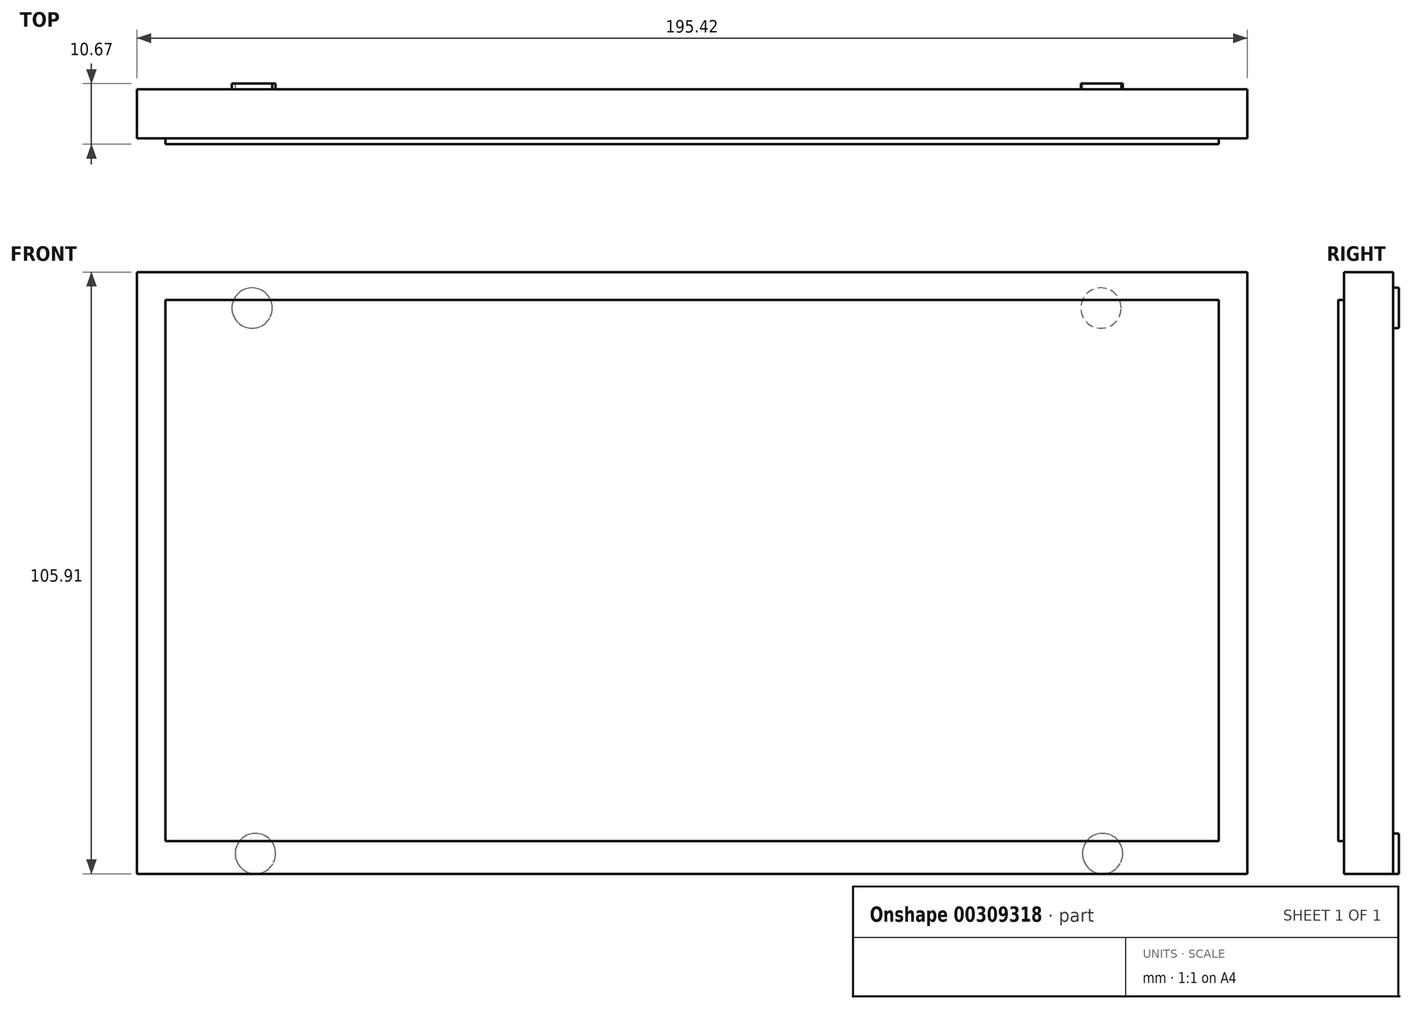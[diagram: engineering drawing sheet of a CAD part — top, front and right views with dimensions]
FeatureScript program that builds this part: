
annotation { "Feature Type Name" : "Feature", "Feature Type Description" : "" }
export const myFeature = defineFeature(function(context is Context, id is Id, definition is map)
    precondition{}
    {
        {
            var Q0;
            Q0=qCreatedBy(makeId("Front.planeOp"),FACE);
            var sketch = newSketch(context, id + "F0", { "sketchPlane" : qUnion([Q0])});
            skLineSegment(sketch, "E0.bottom", {"start": v(-95.26, 50.08) * mm, "end": v(100.16, 50.08) * mm});
            skLineSegment(sketch, "E0.top", {"start": v(-95.26, -55.83) * mm, "end": v(100.16, -55.83) * mm});
            skLineSegment(sketch, "E0.left", {"start": v(-95.26, 50.08) * mm, "end": v(-95.26, -55.83) * mm});
            skLineSegment(sketch, "E0.right", {"start": v(100.16, 50.08) * mm, "end": v(100.16, -55.83) * mm});
            skSolve(sketch);
        }
        {
            var Q0;
            Q0 = qSketchRegion(id + "F0", true);
            var Q1;
            Q1=makeQuery(id+"F0.imprint","IMPRINT",FACE,{"disambiguationData":[TD([[makeQuery(id+"F0.imprint","IMPRINT",EDGE,{"derivedFrom":sQuery(id+"F0.wireOp",EDGE,"Fiwb6U15-hAyw-maav-ymzA-u1ZgBlc6pZ0k.bottom")}),-1.0]])]});
            extrude(context, id + "F1", {"entities" : qUnion([Q0, Q1]), "depth" : 8.64 * mm});
        }
        {
            var Q0;
            Q0=makeQuery(id+"F1.opExtrude","CAP_FACE",FACE,{"disambiguationData":[OSD([sQuery(id+"F0.wireOp",EDGE,"E0.bottom"),sQuery(id+"F0.wireOp",EDGE,"E0.top"),sQuery(id+"F0.wireOp",EDGE,"E0.left"),sQuery(id+"F0.wireOp",EDGE,"E0.right")])],"isStart":false});
            var sketch = newSketch(context, id + "F2", { "sketchPlane" : qUnion([Q0])});
            skLineSegment(sketch, "E1.bottom", {"start": v(-90.23, 45.19) * mm, "end": v(95.12, 45.19) * mm});
            skLineSegment(sketch, "E1.top", {"start": v(-90.23, -50.08) * mm, "end": v(95.12, -50.08) * mm});
            skLineSegment(sketch, "E1.left", {"start": v(-90.23, 45.19) * mm, "end": v(-90.23, -50.08) * mm});
            skLineSegment(sketch, "E1.right", {"start": v(95.12, 45.19) * mm, "end": v(95.12, -50.08) * mm});
            skSolve(sketch);
        }
        {
            var Q0;
            Q0 = qSketchRegion(id + "F2", true);
            extrude(context, id + "F3", {"entities" : qUnion([Q0]), "operationType" : NewBodyOperationType.ADD, "depth" : 1.02 * mm});
        }
        {
            var Q0;
            Q0=makeQuery(id+"F1.opExtrude","CAP_FACE",FACE,{"disambiguationData":[OSD([sQuery(id+"F0.wireOp",EDGE,"E0.bottom"),sQuery(id+"F0.wireOp",EDGE,"E0.top"),sQuery(id+"F0.wireOp",EDGE,"E0.left"),sQuery(id+"F0.wireOp",EDGE,"E0.right")])],"isStart":true});
            var sketch = newSketch(context, id + "F4", { "sketchPlane" : qUnion([Q0])});
            skCircle(sketch, "E2", {"center": v(-74.4, 43.75) * mm, "radius": 3.56 * mm});
            skCircle(sketch, "E3", {"center": v(-74.69, -52.28) * mm, "radius": 3.56 * mm});
            skCircle(sketch, "E4", {"center": v(74.4, -52.28) * mm, "radius": 3.56 * mm});
            skCircle(sketch, "E5", {"center": v(74.97, 43.75) * mm, "radius": 3.56 * mm});
            skSolve(sketch);
        }
        {
            var Q0;
            Q0 = qSketchRegion(id + "F4", true);
            extrude(context, id + "F5", {"entities" : qUnion([Q0]), "operationType" : NewBodyOperationType.ADD, "depth" : 1.02 * mm});
        }
    });
